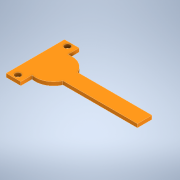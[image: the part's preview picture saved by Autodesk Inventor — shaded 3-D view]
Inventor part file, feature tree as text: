
AUTODESK INVENTOR PART (.ipt)
format: ipt  version: 2021 (Build 250183000, 183)  size: 123,392 bytes
history: native  units: mm
features: other x1, extrude x1, sketch x1
ambient origin geometry x8: Origin, YZ Plane, XZ Plane, XY Plane, X Axis, Y Axis, Z Axis, Center Point
bodies: Solid1 (feature_tree)
feature tree (3):
  other  "<userpath>\Documents\Semestre8\Robótica\Proyecto-Rob\Piezas\ParámetrosGripper.xlsx"
  extrude  "Extrusion1"  Depth=20.0mm
  sketch  "Sketch1"  dims[d0=20.0mm d1=20.0mm d2=80.0mm d3=150.0mm d5=50.0mm d6=15.0mm d7=8.0mm d8=6.0mm d9=8.0mm d10=6.0mm d11=5.0mm d12=0.0mm]
